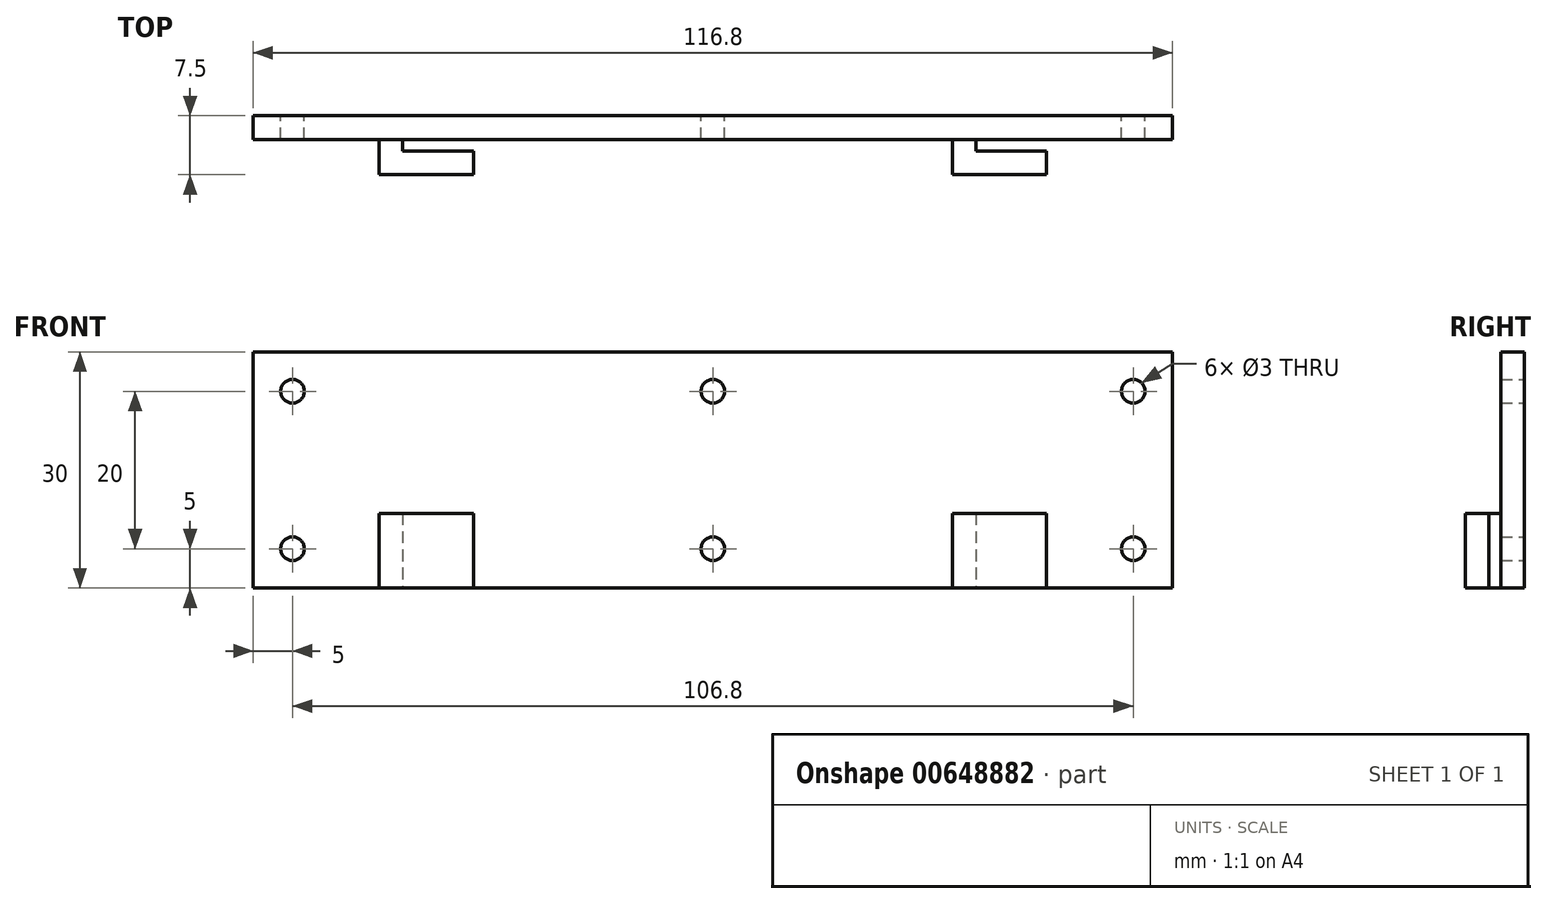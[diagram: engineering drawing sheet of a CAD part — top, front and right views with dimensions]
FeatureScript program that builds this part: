
annotation { "Feature Type Name" : "Feature", "Feature Type Description" : "" }
export const myFeature = defineFeature(function(context is Context, id is Id, definition is map)
    precondition{}
    {
        {
            var Q0;
            Q0=qCreatedBy(makeId("Top.planeOp"),FACE);
            var sketch = newSketch(context, id + "F0", { "sketchPlane" : qUnion([Q0])});
            skLineSegment(sketch, "E0", {"start": v(-24.4, 0) * mm, "end": v(36.4, 0) * mm});
            skLineSegment(sketch, "E1", {"start": v(-24.4, 0) * mm, "end": v(-36.4, 0) * mm});
            skLineSegment(sketch, "E2", {"start": v(-36.4, -3) * mm, "end": v(-36.4, -7.5) * mm});
            skLineSegment(sketch, "E3", {"start": v(-36.4, -7.5) * mm, "end": v(-24.4, -7.5) * mm});
            skLineSegment(sketch, "E4", {"start": v(-24.4, -7.5) * mm, "end": v(-24.4, -4.5) * mm});
            skLineSegment(sketch, "E5", {"start": v(-24.4, -4.5) * mm, "end": v(-33.4, -4.5) * mm});
            skLineSegment(sketch, "E6", {"start": v(-33.4, -4.5) * mm, "end": v(-33.4, -3) * mm});
            skLineSegment(sketch, "E7", {"start": v(-33.4, -3) * mm, "end": v(-24.4, -3) * mm});
            skLineSegment(sketch, "E8", {"start": v(36.4, -3) * mm, "end": v(36.4, -7.5) * mm});
            skLineSegment(sketch, "E9", {"start": v(36.4, -7.5) * mm, "end": v(48.4, -7.5) * mm});
            skLineSegment(sketch, "E10", {"start": v(48.4, -7.5) * mm, "end": v(48.4, -4.5) * mm});
            skLineSegment(sketch, "E11", {"start": v(48.4, -4.5) * mm, "end": v(39.4, -4.5) * mm});
            skLineSegment(sketch, "E12", {"start": v(39.4, -4.5) * mm, "end": v(39.4, -3) * mm});
            skLineSegment(sketch, "E13", {"start": v(39.4, -3) * mm, "end": v(48.4, -3) * mm});
            skLineSegment(sketch, "E14", {"start": v(48.4, 0) * mm, "end": v(36.4, 0) * mm});
            skLineSegment(sketch, "E15", {"start": v(-36.4, 0) * mm, "end": v(-52.4, 0) * mm});
            skLineSegment(sketch, "E16", {"start": v(64.4, 0) * mm, "end": v(48.4, 0) * mm});
            skLineSegment(sketch, "E17", {"start": v(-52.4, 0) * mm, "end": v(-52.4, -3) * mm});
            skLineSegment(sketch, "E18", {"start": v(-52.4, -3) * mm, "end": v(-36.4, -3) * mm});
            skLineSegment(sketch, "E19", {"start": v(64.4, 0) * mm, "end": v(64.4, -3) * mm});
            skLineSegment(sketch, "E20", {"start": v(64.4, -3) * mm, "end": v(48.4, -3) * mm});
            skLineSegment(sketch, "E21", {"start": v(-24.4, -3) * mm, "end": v(36.4, -3) * mm});
            skLineSegment(sketch, "E22", {"start": v(0, 0) * mm, "end": v(0, -3) * mm});
            skSolve(sketch);
        }
        {
            var Q0;
            Q0 = qSketchRegion(id + "F0", true);
            extrude(context, id + "F1", {"entities" : qUnion([Q0]), "depth" : 9.5 * mm, "offsetDistance" : 25 * mm});
        }
        {
            var Q0;
            Q0=makeQuery(id+"F1.opExtrude","CAP_FACE",FACE,{"disambiguationData":[OSD([sQuery(id+"F0.wireOp",EDGE,"E0"),sQuery(id+"F0.wireOp",EDGE,"E1"),sQuery(id+"F0.wireOp",EDGE,"E2"),sQuery(id+"F0.wireOp",EDGE,"E3"),sQuery(id+"F0.wireOp",EDGE,"E4"),sQuery(id+"F0.wireOp",EDGE,"E5"),sQuery(id+"F0.wireOp",EDGE,"E6"),sQuery(id+"F0.wireOp",EDGE,"E7"),sQuery(id+"F0.wireOp",EDGE,"E8"),sQuery(id+"F0.wireOp",EDGE,"E9"),sQuery(id+"F0.wireOp",EDGE,"E10"),sQuery(id+"F0.wireOp",EDGE,"E11"),sQuery(id+"F0.wireOp",EDGE,"E12"),sQuery(id+"F0.wireOp",EDGE,"E13"),sQuery(id+"F0.wireOp",EDGE,"E14"),sQuery(id+"F0.wireOp",EDGE,"E15"),sQuery(id+"F0.wireOp",EDGE,"E16"),sQuery(id+"F0.wireOp",EDGE,"E17"),sQuery(id+"F0.wireOp",EDGE,"E18"),sQuery(id+"F0.wireOp",EDGE,"E19"),sQuery(id+"F0.wireOp",EDGE,"E20"),sQuery(id+"F0.wireOp",EDGE,"E21")])],"isStart":true});
            var sketch = newSketch(context, id + "F2", { "sketchPlane" : qUnion([Q0])});
            skLineSegment(sketch, "E23.bottom", {"start": v(-52.4, 0) * mm, "end": v(64.4, 0) * mm});
            skLineSegment(sketch, "E23.top", {"start": v(-52.4, 3) * mm, "end": v(64.4, 3) * mm});
            skLineSegment(sketch, "E23.left", {"start": v(-52.4, 0) * mm, "end": v(-52.4, 3) * mm});
            skLineSegment(sketch, "E23.right", {"start": v(64.4, 0) * mm, "end": v(64.4, 3) * mm});
            skSolve(sketch);
        }
        {
            var Q0;
            Q0 = qSketchRegion(id + "F2", true);
            extrude(context, id + "F3", {"entities" : qUnion([Q0]), "operationType" : NewBodyOperationType.ADD, "oppositeDirection" : true, "depth" : 30 * mm, "offsetDistance" : 25 * mm});
        }
        {
            var Q0;
            Q0=makeQuery(id+"F3.boolean.opBoolean","MERGE",FACE,{"derivedFrom":[makeQuery(id+"F1.opExtrude","SWEPT_FACE",FACE,{"disambiguationData":[OSD([sQuery(id+"F0.wireOp",EDGE,"E0"),sQuery(id+"F0.wireOp",EDGE,"E1"),sQuery(id+"F0.wireOp",EDGE,"E14"),sQuery(id+"F0.wireOp",EDGE,"E15"),sQuery(id+"F0.wireOp",EDGE,"E16")])]}),makeQuery(id+"F3.opExtrude","SWEPT_FACE",FACE,{"disambiguationData":[OSD([sQuery(id+"F2.wireOp",EDGE,"E23.bottom")])]})]});
            var sketch = newSketch(context, id + "F4", { "sketchPlane" : qUnion([Q0])});
            skCircle(sketch, "E24", {"center": v(47.4, 25) * mm, "radius": 1.5 * mm});
            skCircle(sketch, "E25", {"center": v(-59.4, 25) * mm, "radius": 1.5 * mm});
            skCircle(sketch, "E26", {"center": v(-59.4, 5) * mm, "radius": 1.5 * mm});
            skCircle(sketch, "E27", {"center": v(47.4, 5) * mm, "radius": 1.5 * mm});
            skCircle(sketch, "E28", {"center": v(-6, 25) * mm, "radius": 1.5 * mm});
            skCircle(sketch, "E29", {"center": v(-6, 5) * mm, "radius": 1.5 * mm});
            skSolve(sketch);
        }
        {
            var Q0;
            Q0 = qSketchRegion(id + "F4", true);
            extrude(context, id + "F5", {"entities" : qUnion([Q0]), "operationType" : NewBodyOperationType.REMOVE, "oppositeDirection" : true, "depth" : 25 * mm, "offsetDistance" : 25 * mm});
        }
    });
